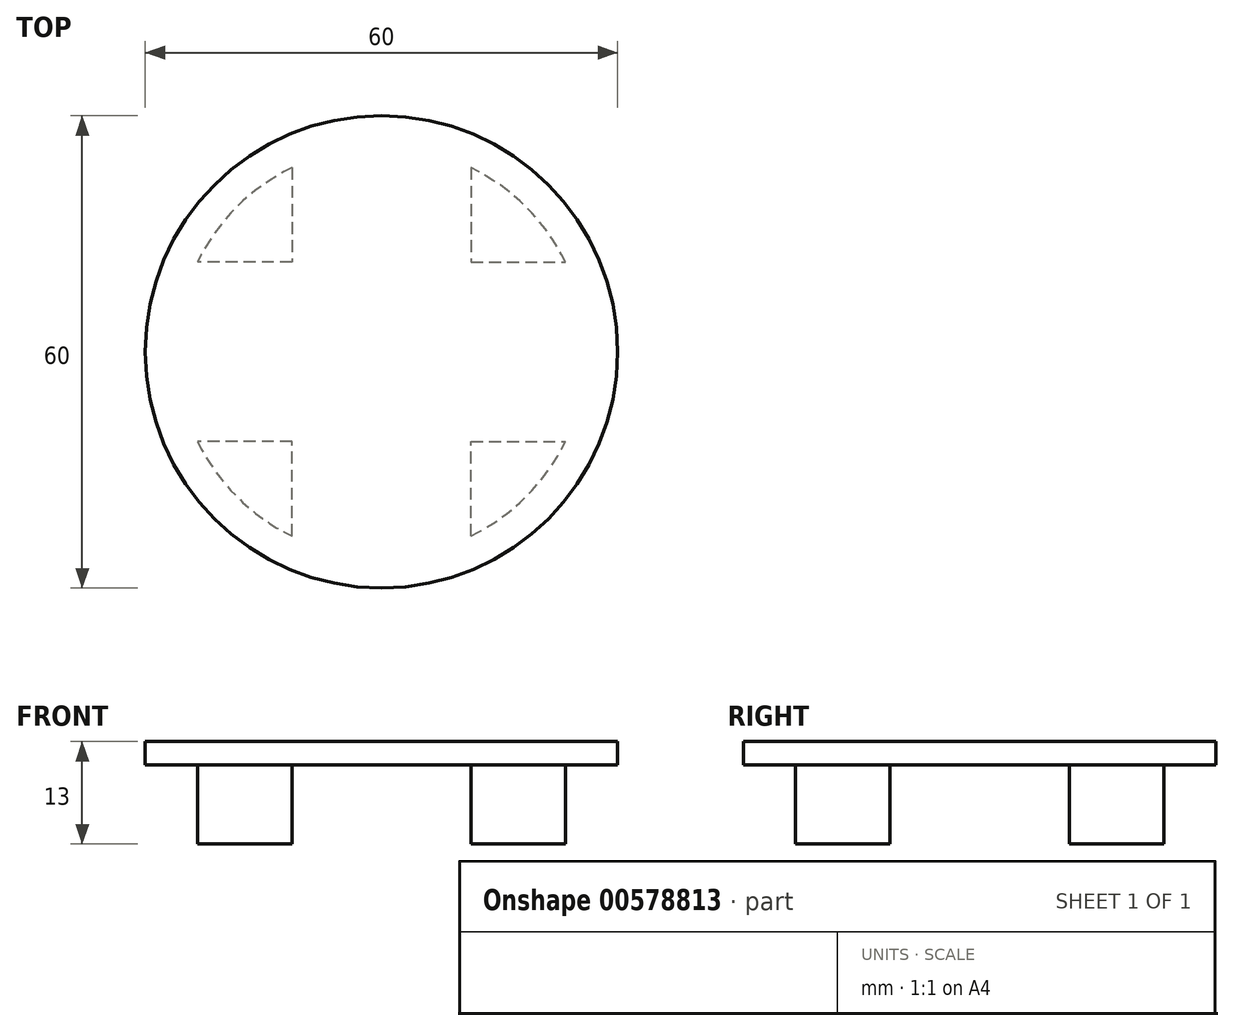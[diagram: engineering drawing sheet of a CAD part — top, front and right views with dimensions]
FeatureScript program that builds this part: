
annotation { "Feature Type Name" : "Feature", "Feature Type Description" : "" }
export const myFeature = defineFeature(function(context is Context, id is Id, definition is map)
    precondition{}
    {
        {
            var Q0;
            Q0=qCreatedBy(makeId("Top.planeOp"),FACE);
            var sketch = newSketch(context, id + "F0", { "sketchPlane" : qUnion([Q0])});
            skCircle(sketch, "E0", {"center": v(0, 0) * mm, "radius": 26 * mm});
            skCircle(sketch, "E1", {"center": v(0, 0) * mm, "radius": 30 * mm});
            skLineSegment(sketch, "E2", {"start": v(-11.38, -23.38) * mm, "end": v(-11.38, -11.38) * mm});
            skLineSegment(sketch, "E3", {"start": v(-11.38, -11.38) * mm, "end": v(-23.38, -11.38) * mm});
            skLineSegment(sketch, "E4", {"start": v(0, 26) * mm, "end": v(0, -26) * mm, "construction": true});
            skLineSegment(sketch, "E5", {"start": v(26, 0) * mm, "end": v(-26, 0) * mm, "construction": true});
            skLineSegment(sketch, "E6.MirrorCS", {"start": v(11.38, -11.38) * mm, "end": v(23.38, -11.38) * mm});
            skLineSegment(sketch, "E7.MirrorCS", {"start": v(11.38, -23.38) * mm, "end": v(11.38, -11.38) * mm});
            skLineSegment(sketch, "E8.MirrorCS", {"start": v(-11.38, 11.38) * mm, "end": v(-23.38, 11.38) * mm});
            skLineSegment(sketch, "E9.MirrorCS", {"start": v(11.38, 23.38) * mm, "end": v(11.38, 11.38) * mm});
            skLineSegment(sketch, "E10.MirrorCS", {"start": v(11.38, 11.38) * mm, "end": v(23.38, 11.38) * mm});
            skLineSegment(sketch, "E11.MirrorCS", {"start": v(-11.38, 23.38) * mm, "end": v(-11.38, 11.38) * mm});
            skSolve(sketch);
        }
        {
            var Q0;
            {var subQ0=sQuery(id+"F0.wireOp",EDGE,"E2");Q0=makeQuery(id+"F0.imprint","IMPRINT",FACE,{"disambiguationData":[TD([[makeQuery(id+"F0.imprint","IMPRINT",EDGE,{"derivedFrom":subQ0}),1.0]])]});}
            var Q1;
            {var subQ0=sQuery(id+"F0.wireOp",EDGE,"E6.MirrorCS");Q1=makeQuery(id+"F0.imprint","IMPRINT",FACE,{"disambiguationData":[TD([[makeQuery(id+"F0.imprint","IMPRINT",EDGE,{"derivedFrom":subQ0}),-1.0]])]});}
            var Q2;
            {var subQ0=sQuery(id+"F0.wireOp",EDGE,"E9.MirrorCS");Q2=makeQuery(id+"F0.imprint","IMPRINT",FACE,{"disambiguationData":[TD([[makeQuery(id+"F0.imprint","IMPRINT",EDGE,{"derivedFrom":subQ0}),1.0]])]});}
            var Q3;
            {var subQ0=sQuery(id+"F0.wireOp",EDGE,"E8.MirrorCS");Q3=makeQuery(id+"F0.imprint","IMPRINT",FACE,{"disambiguationData":[TD([[makeQuery(id+"F0.imprint","IMPRINT",EDGE,{"derivedFrom":subQ0}),-1.0]])]});}
            extrude(context, id + "F1", {"entities" : qUnion([Q0, Q1, Q2, Q3]), "oppositeDirection" : true, "depth" : 10 * mm, "offsetDistance" : 25 * mm});
        }
        {
            var Q0;
            Q0=makeQuery(id+"F0.imprint","IMPRINT",FACE,{"disambiguationData":[TD([[makeQuery(id+"F0.imprint","IMPRINT",EDGE,{"derivedFrom":sQuery(id+"F0.wireOp",EDGE,"E1")}),1.0]])]});
            var Q1;
            {var subQ0=sQuery(id+"F0.wireOp",EDGE,"E8.MirrorCS");Q1=makeQuery(id+"F0.imprint","IMPRINT",FACE,{"disambiguationData":[TD([[makeQuery(id+"F0.imprint","IMPRINT",EDGE,{"derivedFrom":subQ0}),-1.0]])]});}
            var Q2;
            {var subQ0=sQuery(id+"F0.wireOp",EDGE,"E9.MirrorCS");Q2=makeQuery(id+"F0.imprint","IMPRINT",FACE,{"disambiguationData":[TD([[makeQuery(id+"F0.imprint","IMPRINT",EDGE,{"derivedFrom":subQ0}),1.0]])]});}
            var Q3;
            {var subQ0=sQuery(id+"F0.wireOp",EDGE,"E6.MirrorCS");Q3=makeQuery(id+"F0.imprint","IMPRINT",FACE,{"disambiguationData":[TD([[makeQuery(id+"F0.imprint","IMPRINT",EDGE,{"derivedFrom":subQ0}),-1.0]])]});}
            var Q4;
            {var subQ0=sQuery(id+"F0.wireOp",EDGE,"E2");Q4=makeQuery(id+"F0.imprint","IMPRINT",FACE,{"disambiguationData":[TD([[makeQuery(id+"F0.imprint","IMPRINT",EDGE,{"derivedFrom":subQ0}),1.0]])]});}
            var Q5;
            {var subQ3=sQuery(id+"F0.wireOp",EDGE,"E2");Q5=makeQuery(id+"F0.imprint","IMPRINT",FACE,{"disambiguationData":[TD([[makeQuery(id+"F0.imprint","IMPRINT",EDGE,{"derivedFrom":subQ3}),-1.0]])]});}
            extrude(context, id + "F2", {"entities" : qUnion([Q0, Q1, Q2, Q3, Q4, Q5]), "operationType" : NewBodyOperationType.ADD, "depth" : 3 * mm, "offsetDistance" : 25 * mm});
        }
    });
